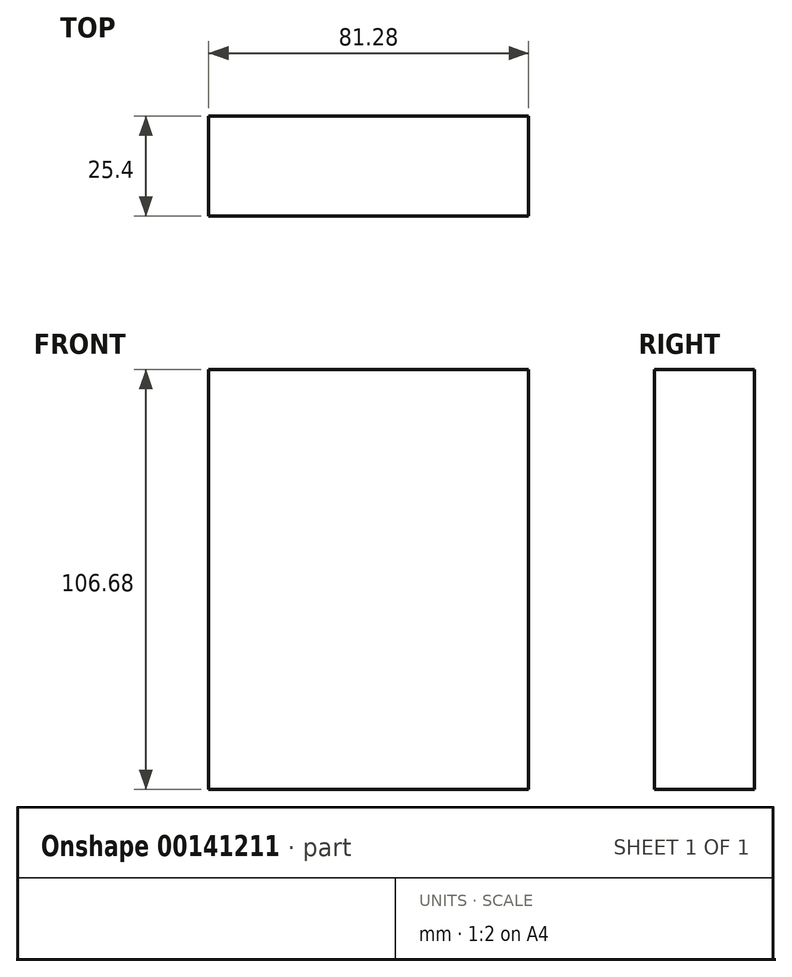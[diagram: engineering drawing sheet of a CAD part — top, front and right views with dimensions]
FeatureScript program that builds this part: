
annotation { "Feature Type Name" : "Feature", "Feature Type Description" : "" }
export const myFeature = defineFeature(function(context is Context, id is Id, definition is map)
    precondition{}
    {
        {
            var Q0;
            Q0=qCreatedBy(makeId("Front.planeOp"),FACE);
            var sketch = newSketch(context, id + "F0", { "sketchPlane" : qUnion([Q0])});
            skLineSegment(sketch, "E0.bottom", {"start": v(0, 0) * mm, "end": v(-81.28, 0) * mm});
            skLineSegment(sketch, "E0.top", {"start": v(0, 106.68) * mm, "end": v(-81.28, 106.68) * mm});
            skLineSegment(sketch, "E0.left", {"start": v(0, 0) * mm, "end": v(0, 106.68) * mm});
            skLineSegment(sketch, "E0.right", {"start": v(-81.28, 0) * mm, "end": v(-81.28, 106.68) * mm});
            skSolve(sketch);
        }
        {
            var Q0;
            Q0 = qSketchRegion(id + "F0", true);
            extrude(context, id + "F1", {"entities" : qUnion([Q0]), "depth" : 25.4 * mm});
        }
    });
